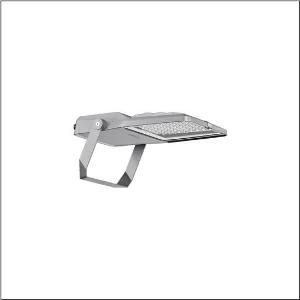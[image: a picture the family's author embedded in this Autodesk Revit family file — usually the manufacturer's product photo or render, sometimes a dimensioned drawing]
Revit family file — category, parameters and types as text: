
# Revit family: floodlight_fl_21_iq_mini___rs12_5xa7771b2b1a_fd88
name_source: partatom
category: Lighting Fixtures
units: mm (PartAtom-declared; Revit-internal decimal feet)

## family parameters
Cut with Voids When Loaded = No
Host = Face
Light Source = No
Part Type = Normal
Room Calculation Point = No
Round Connector Dimension = Use Diameter
Shared = No

## types (1)
- --- (1 x LED, 6300 lm, 45.5 W, 3000K)
    Apparent Load = 46 VA
    CIE Flux Codes = 79 92 99 100 100
    Color Rendering = 70
    Color Temperature = 3000K
    Default Elevation = 1800 mm
    Description = Floodlight FL 21 iQ mini, floodlight, primary light control with lens, of PMMA, primary optical cover: protective disc, of toughened safety glass, transparent, light distribution: RS12, light emission: direct distribution, installation type: surface-mounted, LED, High Power LED, rated luminous flux: 6.300lm, luminous efficacy: 139lm/W, light colour: 730, colour temperature: 3000K, control: Auto-Match, Temp-Guard, Lumen-Switch, Night-Set, Smart-Wire, Light-Fading, Desk-Remote (wireless, voltage-free reading and setting of iQ features in the workshop via application-optimized NFC function/RFID function), optimised constant luminous flux control (CLO 2.0), with terminal, 6-pole, mains connection: 220..240V, AC, 50/60Hz, start of lifetime: 46W, end of service life: 48W, reduction: 22W, luminaire housing, of diecast aluminium, powder-coated, Siteco® metallic grey (DB 702S), corrosivity category C5 mid according to DIN EN ISO 12944, sealing non-destructively replaceable, mounting bracket, of steel, galvanised, powder-coated, Siteco® metallic grey (DB 702S), protection rating (complete): IP66, insulation class (complete): insulation class II (safety insulation), certification: CE, ENEC, VDE, protection symbol: D, impact resistance: IK08, permissible operating ambient temperature: -40..+40°C, permissible operating ambient temperature for outdoor applications: -40..+50°C, standard: DIN EN 12944, LABS conformity tested according to VDMA 24364:2018-05, packaging unit: 1 piece

Light Distribution: RS12
    Height = 70 mm
    Lamp = 1 x LED
    Lamp Light Flux = 6300 lm
    Lamp Power = 45.5 W
    Lamp count = 1
    Length = 485 mm
    Luminous efficacy = 138 lm/W
    Manufacturer = Siteco
    ModVariant = No
    Model = 5XA7771B2B1A
    Mounting Place = Wall
    Mounting Type = Surface mounted
    Number of Poles = 1
    OnlyDefault = Yes
    Power Factor = 1
    Product Name = Floodlight FL 21 iQ mini | RS12
    Product group = floodlight | wall mounted
    ProductGroupID = 2001
    Protection Class = Protection class II
    Protection Degree = IP 66
    RLX_Detail_Level = 1
    RLX_Emergency_Light_Flux = 0 lm
    RLX_Emergency_Type = 0
    RLX_Emergency_Type_DB = No
    RlxData = <blob elided: 90793 chars, md5=4d719108>
    Socket = socket
    Standby Power = 0 W
    System Light Flux = 6300 lm
    System Power = 46 W
    Type Comments = factory setting: luminous flux: 100 % | dim-lin: 254 | 463 mA
    Type Image = l_1006845.jpg
    URL = http://relux.com
    VarID = @adj_100311
    Voltage = 0 V
    Weight = 0.00 kg
    Width = 337 mm

## geometry (parser evidence)
native form markers: Blend x4, Sweep x12
no freeform markers — native parametric forms only
